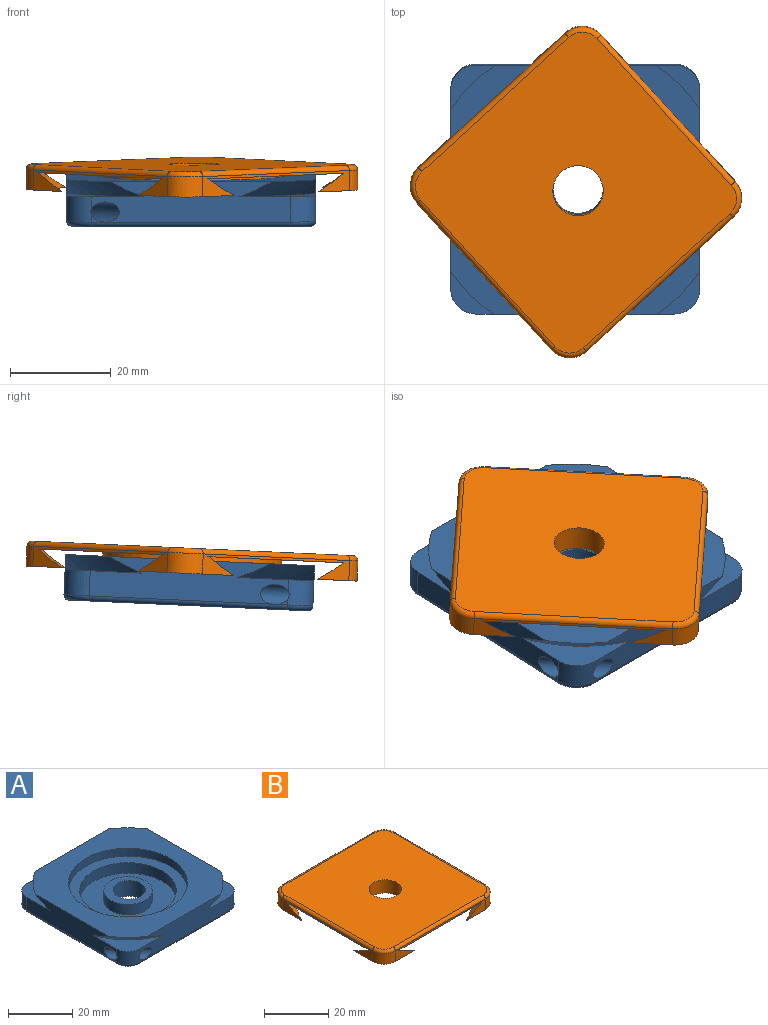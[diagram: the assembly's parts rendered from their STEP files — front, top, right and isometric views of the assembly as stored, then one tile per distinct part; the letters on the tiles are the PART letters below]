
ASSEMBLY  parts=2 mates=1
PART A: 36 faces, bbox 55.1x55.1x9 mm
  f0: plane 2.64x1.28mm, normal (0,-1,0), area 0.9mm2, adj f23,f27,f28
  f1: plane 39.5x8mm, normal (-1,0,0), area 256.9mm2, adj f4,f5,f7,f9,f10,f23,f26,f27
  f2: plane 47.5x47.5mm, normal (0,0,-1), area 2163.7mm2, adj f22,f28,f29,f30,f31,f32,f33,f34
  f3: plane 2.64x1.28mm, normal (-1,0,0), area 0.9mm2, adj f23,f27,f31
  f4: cone r=29.5mm half-angle=45deg, axis (0,0,1), area 71.8mm2, adj f1,f5,f9,f21
  f5: plane 15.28x15.28mm, normal (0,0,1), area 77.9mm2, adj f1,f4,f21,f26
  f6: plane 15.28x15.28mm, normal (0,0,1), area 77.9mm2, adj f12,f19,f21,f24
  f7: cone r=29.5mm half-angle=45deg, axis (0,0,1), area 71.8mm2, adj f1,f9,f10,f20
  f8: cone r=29.5mm half-angle=45deg, axis (0,0,1), area 71.8mm2, adj f9,f11,f19,f20
  f9: plane 49.5x49.5mm, normal (0,0,1), area 1244.9mm2, adj f1,f4,f7,f8,f12,f18,f19,f20
  f10: plane 15.28x15.28mm, normal (0,0,1), area 77.9mm2, adj f1,f7,f20,f27
  f11: plane 15.28x15.28mm, normal (0,0,1), area 77.9mm2, adj f8,f19,f20,f25
  f12: cone r=29.5mm half-angle=45deg, axis (0,0,1), area 71.8mm2, adj f6,f9,f19,f21
  f13: plane 37x37mm, normal (0,0,1), area 368.4mm2, adj f14,f18
  f14: cylinder r=15mm len=30mm, axis (0,0,-1), area 377mm2, adj f13,f15
  f15: plane 30x30mm, normal (0,0,1), area 530.1mm2, adj f14,f16
  f16: cylinder r=7.5mm len=15mm, axis (0,0,-1), area 188.5mm2, adj f15,f17
  f17: plane 15x15mm, normal (0,0,1), area 98.2mm2, adj f16,f22
  f18: cylinder r=18.5mm len=37mm, axis (0,0,-1), area 348.7mm2, adj f9,f13
  f19: plane 39.5x8mm, normal (1,0,0), area 275.4mm2, adj f6,f8,f9,f11,f12,f24,f25,f32
  f20: plane 39.5x8mm, normal (0,-1,0), area 256.9mm2, adj f7,f8,f9,f10,f11,f23,f25,f27
  f21: plane 39.5x8mm, normal (0,1,0), area 275.4mm2, adj f4,f5,f6,f9,f12,f24,f26,f35
  f22: cylinder r=5mm len=10mm, axis (0,0,1), area 188.5mm2, adj f2,f17
  f23: cylinder r=2mm len=13.31mm, axis (0.71,-0.71,0), area 135.7mm2, adj f0,f1,f3,f20,f27
  f24: cylinder r=5mm len=5mm, axis (0,0,1), area 39.3mm2, adj f6,f19,f21,f34
  f25: cylinder r=5mm len=5mm, axis (0,0,-1), area 39.3mm2, adj f11,f19,f20,f30
  f26: cylinder r=5mm len=5mm, axis (0,0,-1), area 39.3mm2, adj f1,f5,f21,f33
  f27: cylinder r=5mm len=5mm, axis (0,0,1), area 38.9mm2, adj f0,f1,f3,f10,f20,f23,f29
  f28: cylinder r=1mm len=39.5mm, axis (-1,0,0), area 62mm2, adj f0,f2,f20,f29,f30
  f29: torus R=4mm, axis (0,0,1), area 11.4mm2, adj f2,f27,f28,f31
  f30: torus R=4mm, axis (0,0,1), area 11.4mm2, adj f2,f25,f28,f32
  f31: cylinder r=1mm len=39.5mm, axis (0,1,0), area 62mm2, adj f1,f2,f3,f29,f33
  f32: cylinder r=1mm len=39.5mm, axis (0,-1,0), area 62mm2, adj f2,f19,f30,f34
  f33: torus R=4mm, axis (0,0,1), area 11.4mm2, adj f2,f26,f31,f35
  f34: torus R=4mm, axis (0,0,1), area 11.4mm2, adj f2,f24,f32,f35
  f35: cylinder r=1mm len=39.5mm, axis (1,0,0), area 62mm2, adj f2,f21,f33,f34
PART B: 29 faces, bbox 55.9x55.9x5 mm
  f0: cone r=30.71mm half-angle=45deg, axis (0,0,1), area 69.5mm2, adj f2,f3,f13,f15
  f1: plane 13.45x13.45mm, normal (0,0,-1), area 63.2mm2, adj f9,f12,f15,f17
  f2: plane 13.45x13.45mm, normal (0,0,-1), area 63.2mm2, adj f0,f13,f15,f20
  f3: plane 49.5x49.5mm, normal (0,0,-1), area 1377.8mm2, adj f0,f4,f5,f9,f11,f12,f13,f14
  f4: cone r=30.71mm half-angle=45deg, axis (0,0,1), area 69.5mm2, adj f3,f7,f13,f14
  f5: cone r=30.71mm half-angle=45deg, axis (0,0,1), area 69.5mm2, adj f3,f6,f12,f14
  f6: plane 13.45x13.45mm, normal (0,0,-1), area 63.2mm2, adj f5,f12,f14,f18
  f7: plane 13.45x13.45mm, normal (0,0,-1), area 63.2mm2, adj f4,f13,f14,f19
  f8: plane 47.5x47.5mm, normal (0,0,1), area 2163.7mm2, adj f16,f21,f22,f23,f24,f25,f26,f27
  f9: cone r=30.71mm half-angle=45deg, axis (0,0,1), area 69.5mm2, adj f1,f3,f12,f15
  f10: plane 35.59x35.59mm, normal (0,0,-1), area 916mm2, adj f11,f16
  f11: cylinder r=17.79mm len=35.59mm, axis (0,0,-1), area 391.3mm2, adj f3,f10
  f12: plane 39.5x4mm, normal (1,0,0), area 53.4mm2, adj f1,f3,f5,f6,f9,f17,f18,f21
  f13: plane 39.5x4mm, normal (-1,0,0), area 53.4mm2, adj f0,f2,f3,f4,f7,f19,f20,f28
  f14: plane 39.5x4mm, normal (0,-1,0), area 53.4mm2, adj f3,f4,f5,f6,f7,f18,f19,f25
  f15: plane 39.5x4mm, normal (0,1,0), area 53.4mm2, adj f0,f1,f2,f3,f9,f17,f20,f24
  f16: cylinder r=5mm len=10mm, axis (0,0,1), area 157.1mm2, adj f8,f10
  f17: cylinder r=5mm len=5mm, axis (0,0,1), area 31.4mm2, adj f1,f12,f15,f22
  f18: cylinder r=5mm len=5mm, axis (0,0,-1), area 31.4mm2, adj f6,f12,f14,f23
  f19: cylinder r=5mm len=5mm, axis (0,0,1), area 31.4mm2, adj f7,f13,f14,f27
  f20: cylinder r=5mm len=5mm, axis (0,0,-1), area 31.4mm2, adj f2,f13,f15,f26
  f21: cylinder r=1mm len=39.5mm, axis (0,-1,0), area 62mm2, adj f8,f12,f22,f23
  f22: torus R=4mm, axis (0,0,-1), area 11.4mm2, adj f8,f17,f21,f24
  f23: torus R=4mm, axis (0,0,-1), area 11.4mm2, adj f8,f18,f21,f25
  f24: cylinder r=1mm len=39.5mm, axis (1,0,0), area 62mm2, adj f8,f15,f22,f26
  f25: cylinder r=1mm len=39.5mm, axis (-1,0,0), area 62mm2, adj f8,f14,f23,f27
  f26: torus R=4mm, axis (0,0,-1), area 11.4mm2, adj f8,f20,f24,f28
  f27: torus R=4mm, axis (0,0,-1), area 11.4mm2, adj f8,f19,f25,f28
  f28: cylinder r=1mm len=39.5mm, axis (0,1,0), area 62mm2, adj f8,f13,f26,f27
PLACE A rot(axis=(1,0,0),2.6deg) t=(-39.51,6.14,0.27)mm
PLACE B rot(axis=(0.06,-0.02,1),42.6deg) t=(-39.36,5.75,0.62)mm
MATE cylindrical B.f16 <-> A.f22  axis (0,-0.05,1) through (-38.95,5.94,4.63)mm
